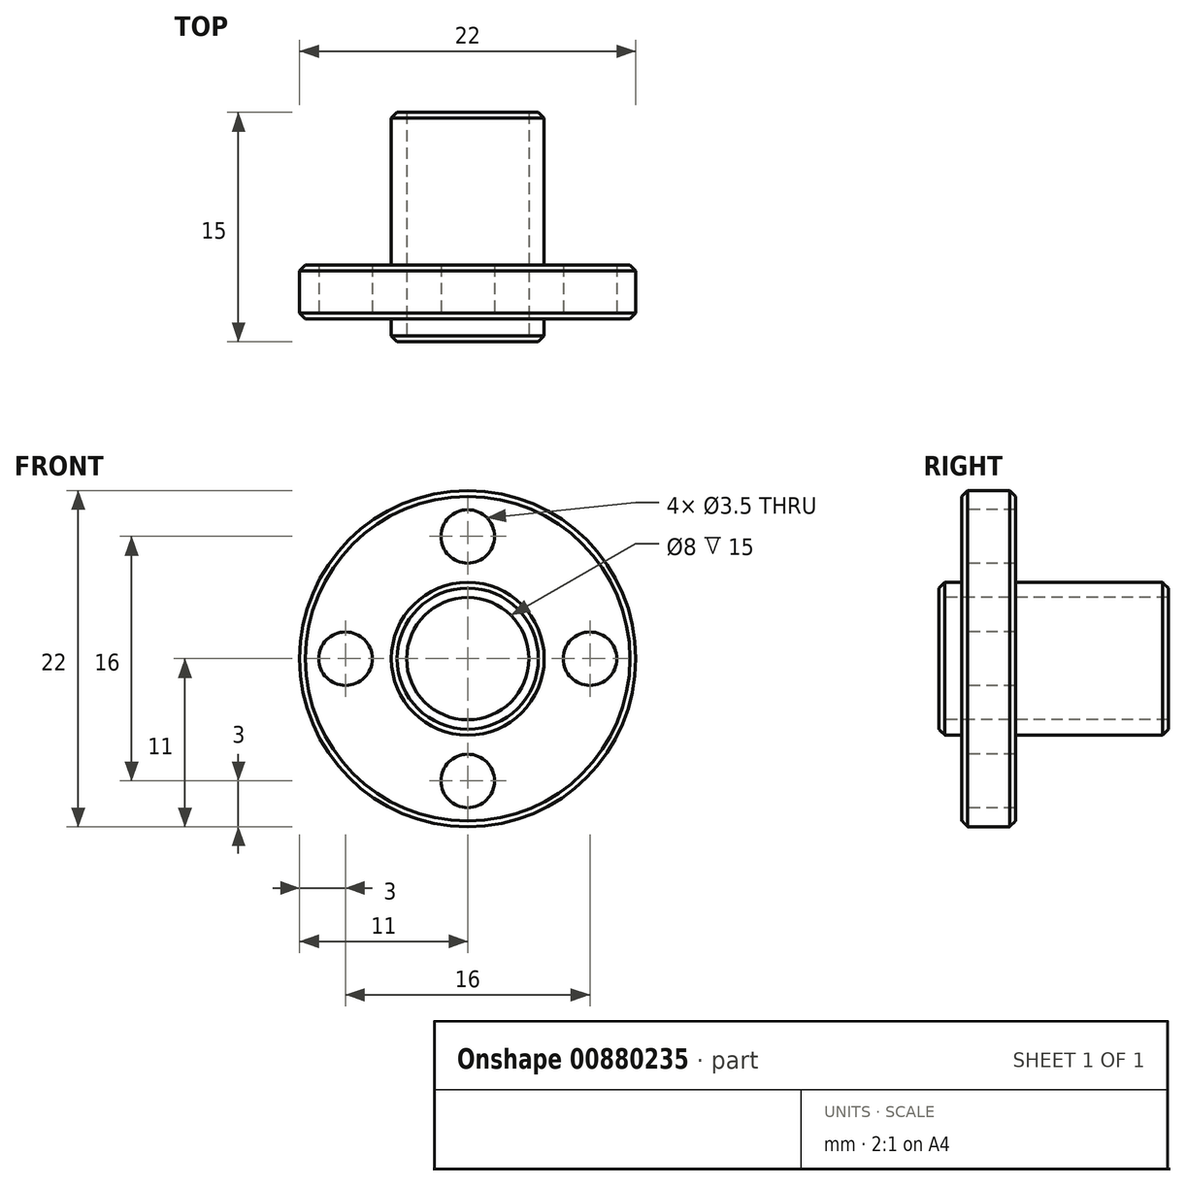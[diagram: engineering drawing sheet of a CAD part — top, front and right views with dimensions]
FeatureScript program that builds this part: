
annotation { "Feature Type Name" : "Feature", "Feature Type Description" : "" }
export const myFeature = defineFeature(function(context is Context, id is Id, definition is map)
    precondition{}
    {
        {
            var Q0;
            Q0=qCreatedBy(makeId("Front.planeOp"),FACE);
            var sketch = newSketch(context, id + "F0", { "sketchPlane" : qUnion([Q0])});
            skCircle(sketch, "E0", {"center": v(0, 0) * mm, "radius": 11 * mm});
            skSolve(sketch);
        }
        {
            var Q0;
            Q0=qSketchRegion(id+"F0",true);
            extrude(context, id + "F1", {"entities" : qUnion([Q0]), "depth" : 3.5 * mm});
        }
        {
            var Q0;
            Q0=makeQuery(id+"F1.opExtrude","CAP_FACE",FACE,{"disambiguationData":[OSD([sQuery(id+"F0.wireOp",EDGE,"E0")])],"isStart":false});
            var sketch = newSketch(context, id + "F2", { "sketchPlane" : qUnion([Q0])});
            skCircle(sketch, "E1", {"center": v(0, 0) * mm, "radius": 5 * mm});
            skSolve(sketch);
        }
        {
            var Q0;
            Q0=qSketchRegion(id+"F2",true);
            extrude(context, id + "F3", {"entities" : qUnion([Q0]), "operationType" : NewBodyOperationType.ADD, "depth" : 1.5 * mm});
        }
        {
            var Q0;
            Q0=makeQuery(id+"F1.opExtrude","CAP_FACE",FACE,{"disambiguationData":[OSD([sQuery(id+"F0.wireOp",EDGE,"E0")])],"isStart":true});
            var sketch = newSketch(context, id + "F4", { "sketchPlane" : qUnion([Q0])});
            skCircle(sketch, "E2", {"center": v(0, 0) * mm, "radius": 5 * mm});
            skSolve(sketch);
        }
        {
            var Q0;
            Q0=qSketchRegion(id+"F4",true);
            extrude(context, id + "F5", {"entities" : qUnion([Q0]), "operationType" : NewBodyOperationType.ADD, "depth" : 10 * mm});
        }
        {
            var Q0;
            Q0=makeQuery(id+"F3.opExtrude","CAP_FACE",FACE,{"disambiguationData":[OSD([sQuery(id+"F2.wireOp",EDGE,"E1")])],"isStart":false});
            var sketch = newSketch(context, id + "F6", { "sketchPlane" : qUnion([Q0])});
            skCircle(sketch, "E3", {"center": v(0, 0) * mm, "radius": 4 * mm});
            skSolve(sketch);
        }
        {
            var Q0;
            Q0=qSketchRegion(id+"F6",true);
            extrude(context, id + "F7", {"entities" : qUnion([Q0]), "operationType" : NewBodyOperationType.REMOVE, "oppositeDirection" : true, "depth" : 25.4 * mm});
        }
        {
            var Q0;
            Q0=makeQuery(id+"F1.opExtrude","CAP_FACE",FACE,{"disambiguationData":[OSD([sQuery(id+"F0.wireOp",EDGE,"E0")])],"isStart":false});
            var sketch = newSketch(context, id + "F8", { "sketchPlane" : qUnion([Q0])});
            skCircle(sketch, "E4", {"center": v(-8, 0) * mm, "radius": 1.75 * mm});
            skCircle(sketch, "E5", {"center": v(8, 0) * mm, "radius": 1.75 * mm});
            skCircle(sketch, "E6", {"center": v(0, 8) * mm, "radius": 1.75 * mm});
            skCircle(sketch, "E7", {"center": v(0, -8) * mm, "radius": 1.75 * mm});
            skCircle(sketch, "E8", {"center": v(0, 0) * mm, "radius": 8 * mm, "construction": true});
            skSolve(sketch);
        }
        {
            var Q0;
            Q0=qSketchRegion(id+"F8",true);
            extrude(context, id + "F9", {"entities" : qUnion([Q0]), "operationType" : NewBodyOperationType.REMOVE, "oppositeDirection" : true, "depth" : 25.4 * mm});
        }
        {
            var Q0;
            Q0=makeQuery(id+"F1.opExtrude","SWEPT_FACE",FACE,{"disambiguationData":[OSD([sQuery(id+"F0.wireOp",EDGE,"E0")])]});
            chamfer(context, id + "F10", {"entities" : qUnion([Q0]), "width" : 0.38 * mm, "tangentPropagation" : true});
        }
        {
            var Q0;
            Q0=makeQuery(id+"F5.opExtrude","CAP_EDGE",EDGE,{"disambiguationData":[OSD([sQuery(id+"F4.wireOp",EDGE,"E2")])],"isStart":false});
            var Q1;
            Q1=makeQuery(id+"F3.opExtrude","CAP_EDGE",EDGE,{"disambiguationData":[OSD([sQuery(id+"F2.wireOp",EDGE,"E1")])],"isStart":false});
            chamfer(context, id + "F11", {"entities" : qUnion([Q0, Q1]), "width" : 0.38 * mm, "tangentPropagation" : true});
        }
    });
